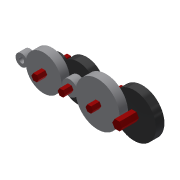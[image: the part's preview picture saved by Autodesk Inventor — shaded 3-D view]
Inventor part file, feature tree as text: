
AUTODESK INVENTOR PART (.ipt)
format: ipt  version: 2013 (Build 170138000, 138)  size: 201,728 bytes
history: native  units: in
note: dims shown in document units (in); Inventor stores cm internally (conversion verified against a paired STEP export)
features: extrude x3, sketch x1
ambient origin geometry x8: Origin, YZ Plane, XZ Plane, XY Plane, X Axis, Y Axis, Z Axis, Center Point
bodies: Solid1 (feature_tree), Solid2 (feature_tree), Solid3 (feature_tree)
feature tree (4):
  sketch  "Sketch1"  dims[d0=2.1in d1=0.375in d2=1.1in d3=2.2in d4=1.553in d5=0.9in d6=0.7in d7=1.303in d8=2.6in d9=1.653in d10=0.375in d11=0.5in d12=0.0in d13=0.5in d14=0.0in d15=0.375in d16=2.0in d17=0.0in d18=0.315in d19=0.0787in d20=0.0787in d21=0.9in d22=2.6in d23=1.653in d24=0.5in]
  extrude  "Extrusion1"  Depth=0.375in
  extrude  "Extrusion2"  Depth=1.1in
  extrude  "Extrusion3"  Depth=2.2in
